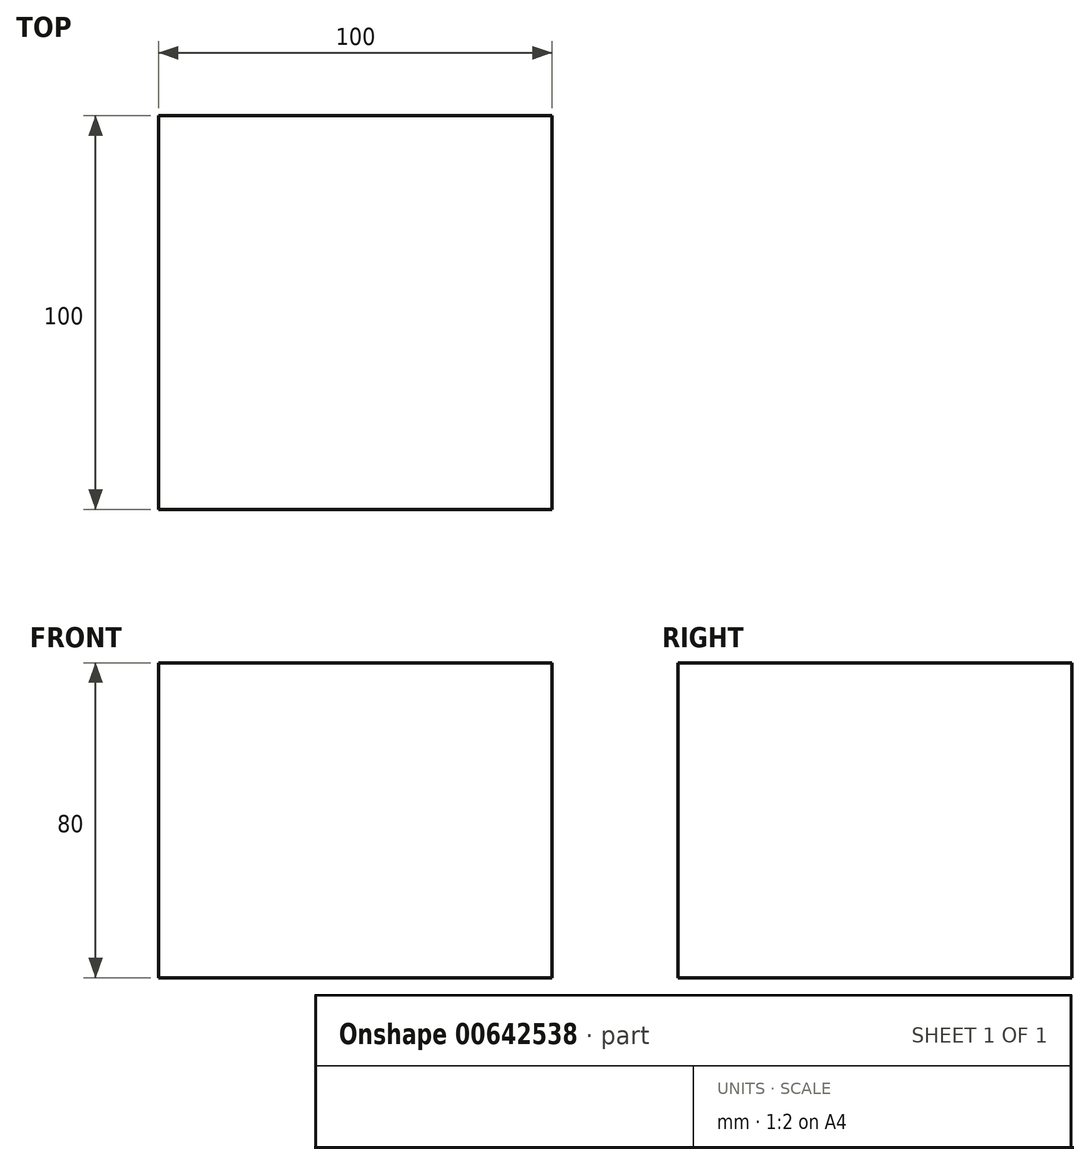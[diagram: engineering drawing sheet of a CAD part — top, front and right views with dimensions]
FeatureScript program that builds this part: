
annotation { "Feature Type Name" : "Feature", "Feature Type Description" : "" }
export const myFeature = defineFeature(function(context is Context, id is Id, definition is map)
    precondition{}
    {
        {
            var Q0;
            Q0=qCreatedBy(makeId("Top.planeOp"),FACE);
            var sketch = newSketch(context, id + "F0", { "sketchPlane" : qUnion([Q0])});
            skLineSegment(sketch, "E0.bottom", {"start": v(50, 50) * mm, "end": v(-50, 50) * mm});
            skLineSegment(sketch, "E0.top", {"start": v(50, -50) * mm, "end": v(-50, -50) * mm});
            skLineSegment(sketch, "E0.left", {"start": v(50, 50) * mm, "end": v(50, -50) * mm});
            skLineSegment(sketch, "E0.right", {"start": v(-50, 50) * mm, "end": v(-50, -50) * mm});
            skPoint(sketch, "E0.middle", {"position": v(0, 0) * mm});
            skSolve(sketch);
        }
        {
            var Q0;
            Q0=makeQuery(id+"F0.imprint","IMPRINT",FACE,{"disambiguationData":[TD([[makeQuery(id+"F0.imprint","IMPRINT",EDGE,{"derivedFrom":sQuery(id+"F0.wireOp",EDGE,"E0.bottom")}),1.0]])]});
            extrude(context, id + "F1", {"entities" : qUnion([Q0]), "depth" : 80 * mm, "offsetDistance" : 25 * mm});
        }
    });
